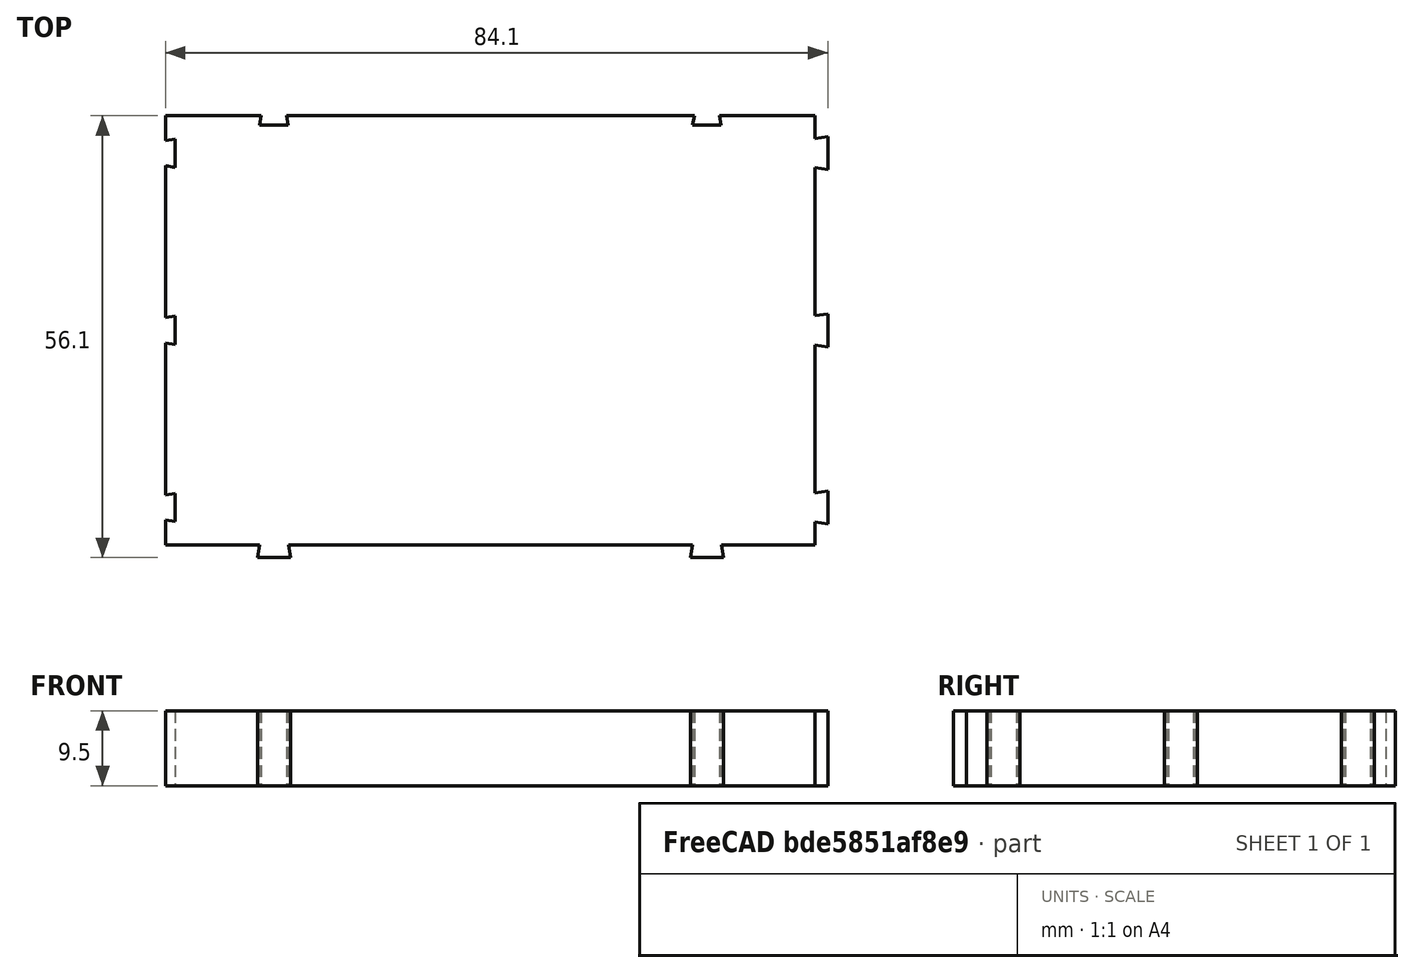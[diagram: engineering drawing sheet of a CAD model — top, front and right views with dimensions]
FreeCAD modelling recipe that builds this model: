
FCSTD DOCUMENT  (FreeCAD 0.18R15969 (Git))
Label: feature_breadboard
License: All rights reserved
LicenseURL: http://en.wikipedia.org/wiki/All_rights_reserved
objects: Sketcher::SketchObject×1, PartDesign::Pad×1, PartDesign::Body×1
note: 4 computed .brp shape members not serialized (recipe doc carries the construction recipe); baked Part::Feature solids carry a one-line shape summary decoded from their .brp

FEATURE [Sketcher::SketchObject] Sketch
  MapMode = 5
  Support = -> [XY_Plane]
  sketch-geometry (85):
    g0: LineSegment [constr] StartX=-41.25 StartY=-27.25 StartZ=0 EndX=41.25 EndY=-27.25 EndZ=0
    g1: LineSegment [constr] StartX=41.25 StartY=-27.25 StartZ=0 EndX=41.25 EndY=27.25 EndZ=0
    g2: LineSegment [constr] StartX=41.25 StartY=27.25 StartZ=0 EndX=-41.25 EndY=27.25 EndZ=0
    g3: LineSegment [constr] StartX=-41.25 StartY=27.25 StartZ=0 EndX=-41.25 EndY=-27.25 EndZ=0
    g4: LineSegment [constr] StartX=-41.25 StartY=27.25 StartZ=0 EndX=0 EndY=0 EndZ=0
    g5: LineSegment [constr] StartX=0 StartY=0 StartZ=0 EndX=41.25 EndY=27.25 EndZ=0
    g6: LineSegment [constr] StartX=0 StartY=0 StartZ=0 EndX=-41.25 EndY=-27.25 EndZ=0
    g7: LineSegment StartX=-41.25 StartY=27.25 StartZ=0 EndX=-29.1 EndY=27.25 EndZ=0
    g8: LineSegment StartX=-29.1 StartY=27.25 StartZ=0 EndX=-29.3 EndY=26.05 EndZ=0
    g9: LineSegment StartX=-29.3 StartY=26.05 StartZ=0 EndX=-25.7 EndY=26.05 EndZ=0
    g10: LineSegment StartX=-25.7 StartY=26.05 StartZ=0 EndX=-25.9 EndY=27.25 EndZ=0
    g11: LineSegment StartX=-25.9 StartY=27.25 StartZ=0 EndX=25.9 EndY=27.25 EndZ=0
    g12: LineSegment StartX=25.9 StartY=27.25 StartZ=0 EndX=25.7 EndY=26.05 EndZ=0
    g13: LineSegment StartX=25.7 StartY=26.05 StartZ=0 EndX=29.3 EndY=26.05 EndZ=0
    g14: LineSegment StartX=29.3 StartY=26.05 StartZ=0 EndX=29.1 EndY=27.25 EndZ=0
    g15: LineSegment StartX=29.1 StartY=27.25 StartZ=0 EndX=41.25 EndY=27.25 EndZ=0
    g16: LineSegment StartX=-41.25 StartY=27.25 StartZ=0 EndX=-41.25 EndY=24.1 EndZ=0
    g17: LineSegment StartX=-41.25 StartY=24.1 StartZ=0 EndX=-40.05 EndY=24.3 EndZ=0
    g18: LineSegment StartX=-40.05 StartY=24.3 StartZ=0 EndX=-40.05 EndY=20.7 EndZ=0
    g19: LineSegment StartX=-40.05 StartY=20.7 StartZ=0 EndX=-41.25 EndY=20.9 EndZ=0
    g20: LineSegment StartX=-41.25 StartY=20.9 StartZ=0 EndX=-41.25 EndY=1.6 EndZ=0
    g21: LineSegment StartX=-41.25 StartY=1.6 StartZ=0 EndX=-40.05 EndY=1.8 EndZ=0
    g22: LineSegment StartX=-40.05 StartY=1.8 StartZ=0 EndX=-40.05 EndY=-1.8 EndZ=0
    g23: LineSegment StartX=-40.05 StartY=-1.8 StartZ=0 EndX=-41.25 EndY=-1.6 EndZ=0
    g24: LineSegment [constr] StartX=-40.05 StartY=-1.8 StartZ=0 EndX=-41.25 EndY=1.6 EndZ=0
    g25: LineSegment [constr] StartX=-40.05 StartY=20.7 StartZ=0 EndX=-41.25 EndY=24.1 EndZ=0
    g26: LineSegment [constr] StartX=-29.3 StartY=26.05 StartZ=0 EndX=-25.9 EndY=27.25 EndZ=0
    g27: LineSegment [constr] StartX=25.7 StartY=26.05 StartZ=0 EndX=29.1 EndY=27.25 EndZ=0
    g28: LineSegment StartX=-41.25 StartY=-1.6 StartZ=0 EndX=-41.25 EndY=-20.9 EndZ=0
    g29: LineSegment StartX=-41.25 StartY=-20.9 StartZ=0 EndX=-40.05 EndY=-20.7 EndZ=0
    g30: LineSegment StartX=-40.05 StartY=-20.7 StartZ=0 EndX=-40.05 EndY=-24.3 EndZ=0
    g31: LineSegment StartX=-40.05 StartY=-24.3 StartZ=0 EndX=-41.25 EndY=-24.1 EndZ=0
    g32: LineSegment StartX=-41.25 StartY=-24.1 StartZ=0 EndX=-41.25 EndY=-27.25 EndZ=0
    g33: LineSegment [constr] StartX=-41.25 StartY=-20.9 StartZ=0 EndX=-40.05 EndY=-24.3 EndZ=0
    g34: LineSegment [constr] StartX=0 StartY=0 StartZ=0 EndX=-40.05 EndY=1.8 EndZ=0
    g35: LineSegment [constr] StartX=0 StartY=0 StartZ=0 EndX=-40.05 EndY=-1.8 EndZ=0
    g36: LineSegment [constr] StartX=-40.05 StartY=20.7 StartZ=0 EndX=0 EndY=22.5 EndZ=0
    g37: LineSegment [constr] StartX=0 StartY=22.5 StartZ=0 EndX=-40.05 EndY=24.3 EndZ=0
    g38: LineSegment [constr] StartX=-40.05 StartY=-20.7 StartZ=0 EndX=0 EndY=-22.5 EndZ=0
    g39: LineSegment [constr] StartX=-40.05 StartY=-24.3 StartZ=0 EndX=0 EndY=-22.5 EndZ=0
    g40: LineSegment [constr] StartX=0 StartY=-22.5 StartZ=0 EndX=0 EndY=0 EndZ=0
    g41: LineSegment [constr] StartX=0 StartY=0 StartZ=0 EndX=0 EndY=22.5 EndZ=0
    g42: LineSegment [constr] StartX=-29.3 StartY=26.05 StartZ=0 EndX=-27.5 EndY=-27.25 EndZ=0
    g43: LineSegment [constr] StartX=-27.5 StartY=-27.25 StartZ=0 EndX=-25.7 EndY=26.05 EndZ=0
    g44: LineSegment [constr] StartX=29.3 StartY=26.05 StartZ=0 EndX=27.5 EndY=-27.25 EndZ=0
    g45: LineSegment [constr] StartX=25.7 StartY=26.05 StartZ=0 EndX=27.5 EndY=-27.25 EndZ=0
    g46: LineSegment [constr] StartX=-27.5 StartY=-27.25 StartZ=0 EndX=0 EndY=0 EndZ=0
    g47: LineSegment [constr] StartX=0 StartY=0 StartZ=0 EndX=27.5 EndY=-27.25 EndZ=0
    g48: LineSegment StartX=41.25 StartY=27.25 StartZ=0 EndX=41.25 EndY=24.35 EndZ=0
    g49: LineSegment StartX=41.25 StartY=24.35 StartZ=0 EndX=42.85 EndY=24.6 EndZ=0
    g50: LineSegment StartX=42.85 StartY=24.6 StartZ=0 EndX=42.85 EndY=20.4 EndZ=0
    g51: LineSegment StartX=42.85 StartY=20.4 StartZ=0 EndX=41.25 EndY=20.65 EndZ=0
    g52: LineSegment StartX=41.25 StartY=20.65 StartZ=0 EndX=41.25 EndY=1.85 EndZ=0
    g53: LineSegment StartX=41.25 StartY=1.85 StartZ=0 EndX=42.85 EndY=2.1 EndZ=0
    g54: LineSegment StartX=42.85 StartY=2.1 StartZ=0 EndX=42.85 EndY=-2.1 EndZ=0
    g55: LineSegment StartX=42.85 StartY=-2.1 StartZ=0 EndX=41.25 EndY=-1.85 EndZ=0
    g56: LineSegment StartX=41.25 StartY=-1.85 StartZ=0 EndX=41.25 EndY=-20.65 EndZ=0
    g57: LineSegment StartX=41.25 StartY=-20.65 StartZ=0 EndX=42.85 EndY=-20.4 EndZ=0
    g58: LineSegment StartX=42.85 StartY=-20.4 StartZ=0 EndX=42.85 EndY=-24.6 EndZ=0
    g59: LineSegment StartX=42.85 StartY=-24.6 StartZ=0 EndX=41.25 EndY=-24.35 EndZ=0
    g60: LineSegment StartX=41.25 StartY=-24.35 StartZ=0 EndX=41.25 EndY=-27.25 EndZ=0
    g61: LineSegment StartX=-41.25 StartY=-27.25 StartZ=0 EndX=-29.35 EndY=-27.25 EndZ=0
    g62: LineSegment StartX=-29.35 StartY=-27.25 StartZ=0 EndX=-29.6 EndY=-28.85 EndZ=0
    g63: LineSegment StartX=-29.6 StartY=-28.85 StartZ=0 EndX=-25.4 EndY=-28.85 EndZ=0
    g64: LineSegment StartX=-25.4 StartY=-28.85 StartZ=0 EndX=-25.65 EndY=-27.25 EndZ=0
    g65: LineSegment StartX=-25.65 StartY=-27.25 StartZ=0 EndX=25.65 EndY=-27.25 EndZ=0
    g66: LineSegment StartX=25.65 StartY=-27.25 StartZ=0 EndX=25.4 EndY=-28.85 EndZ=0
    g67: LineSegment StartX=25.4 StartY=-28.85 StartZ=0 EndX=29.6 EndY=-28.85 EndZ=0
    g68: LineSegment StartX=29.6 StartY=-28.85 StartZ=0 EndX=29.35 EndY=-27.25 EndZ=0
    g69: LineSegment StartX=29.35 StartY=-27.25 StartZ=0 EndX=41.25 EndY=-27.25 EndZ=0
    g70: LineSegment [constr] StartX=-29.6 StartY=-28.85 StartZ=0 EndX=-27.5 EndY=-27.25 EndZ=0
    g71: LineSegment [constr] StartX=-27.5 StartY=-27.25 StartZ=0 EndX=-25.4 EndY=-28.85 EndZ=0
    g72: LineSegment [constr] StartX=25.4 StartY=-28.85 StartZ=0 EndX=27.5 EndY=-27.25 EndZ=0
    g73: LineSegment [constr] StartX=27.5 StartY=-27.25 StartZ=0 EndX=29.6 EndY=-28.85 EndZ=0
    g74: LineSegment [constr] StartX=42.85 StartY=-20.4 StartZ=0 EndX=0 EndY=-22.5 EndZ=0
    g75: LineSegment [constr] StartX=0 StartY=-22.5 StartZ=0 EndX=42.85 EndY=-24.6 EndZ=0
    g76: LineSegment [constr] StartX=42.85 StartY=-2.1 StartZ=0 EndX=0 EndY=0 EndZ=0
    g77: LineSegment [constr] StartX=0 StartY=0 StartZ=0 EndX=42.85 EndY=2.1 EndZ=0
    g78: LineSegment [constr] StartX=42.85 StartY=20.4 StartZ=0 EndX=0 EndY=22.5 EndZ=0
    g79: LineSegment [constr] StartX=0 StartY=22.5 StartZ=0 EndX=42.85 EndY=24.6 EndZ=0
    g80: LineSegment [constr] StartX=-29.35 StartY=-27.25 StartZ=0 EndX=-25.4 EndY=-28.85 EndZ=0
    g81: LineSegment [constr] StartX=25.65 StartY=-27.25 StartZ=0 EndX=29.6 EndY=-28.85 EndZ=0
    g82: LineSegment [constr] StartX=41.25 StartY=-24.35 StartZ=0 EndX=42.85 EndY=-20.4 EndZ=0
    g83: LineSegment [constr] StartX=41.25 StartY=-1.85 StartZ=0 EndX=42.85 EndY=2.1 EndZ=0
    g84: LineSegment [constr] StartX=41.25 StartY=20.65 StartZ=0 EndX=42.85 EndY=24.6 EndZ=0
  constraints (226):
    c: Coincident(g0,g1)
    c: Coincident(g1,g2)
    c: Coincident(g2,g3)
    c: Coincident(g3,g0)
    c: Horizontal(g0)
    c: Horizontal(g2)
    c: Vertical(g1)
    c: Vertical(g3)
    c: DistanceX(g2,g2) = 82.5
    c: DistanceY(g1,g1) = 54.5
    c: Coincident(g4,g2)
    c: Coincident(g5,g4)
    c: Coincident(g5,g1)
    c: Coincident(g6,g4)
    c: Coincident(g6,g0)
    c: Equal(g6,g4)
    c: Equal(g4,g5)
    c: Coincident(g2,g7)
    c: Coincident(g7,g8)
    c: Coincident(g8,g9)
    c: Horizontal(g9)
    c: Coincident(g9,g10)
    c: Coincident(g10,g11)
    c: Coincident(g11,g12)
    c: Coincident(g12,g13)
    c: Horizontal(g13)
    c: Coincident(g13,g14)
    c: Coincident(g14,g15)
    c: Coincident(g15,g1)
    c: PointOnObject(g14,g2)
    c: PointOnObject(g11,g2)
    c: PointOnObject(g10,g2)
    c: PointOnObject(g7,g2)
    c: Equal(g8,g10)
    c: Equal(g12,g14)
    c: Coincident(g7,g16)
    c: Coincident(g16,g17)
    c: Coincident(g17,g18)
    c: Vertical(g18)
    c: Coincident(g18,g19)
    c: Coincident(g19,g20)
    c: Coincident(g20,g21)
    c: Coincident(g21,g22)
    c: Vertical(g22)
    c: Coincident(g22,g23)
    c: PointOnObject(g23,g3)
    c: PointOnObject(g20,g3)
    c: PointOnObject(g19,g3)
    c: PointOnObject(g16,g3)
    c: Equal(g8,g17)
    c: Equal(g17,g19)
    c: Equal(g19,g21)
    c: Equal(g21,g23)
    c: Equal(g22,g18)
    c: Equal(g18,g9)
    c: Equal(g9,g13)
    c: Coincident(g24,g22)
    c: Coincident(g24,g20)
    c: Coincident(g25,g18)
    c: Coincident(g25,g16)
    c: Coincident(g26,g8)
    c: Coincident(g26,g10)
    c: Coincident(g27,g12)
    c: Coincident(g27,g14)
    c: Equal(g26,g27)
    c: Equal(g27,g25)
    c: Equal(g25,g24)
    c: Coincident(g23,g28)
    c: Coincident(g28,g29)
    c: Coincident(g29,g30)
    c: Vertical(g30)
    c: Coincident(g30,g31)
    c: Coincident(g31,g32)
    c: Coincident(g32,g0)
    c: PointOnObject(g31,g3)
    c: PointOnObject(g28,g3)
    c: Equal(g30,g22)
    c: Equal(g29,g31)
    c: Equal(g31,g23)
    c: Coincident(g33,g28)
    c: Coincident(g33,g30)
    c: Equal(g33,g24)
    c: Coincident(g34,g4)
    c: Coincident(g34,g21)
    c: Coincident(g35,g4)
    c: Coincident(g35,g22)
    c: Coincident(g36,g18)
    c: PointOnObject(g36,g-2)
    c: Coincident(g37,g36)
    c: Coincident(g37,g17)
    c: Coincident(g38,g29)
    c: PointOnObject(g38,g-2)
    c: Coincident(g39,g30)
    c: Coincident(g39,g38)
    c: Coincident(g40,g38)
    c: Coincident(g40,g4)
    c: Coincident(g41,g4)
    c: Coincident(g41,g36)
    c: Equal(g41,g40)
    c: DistanceY(g38,g36) = 45
    c: DistanceY(g19,g16) = 3.2
    c: DistanceY(g18,g18) = 3.6
    c: DistanceX(g19,g19) = 1.2
    c: Coincident(g42,g8)
    c: PointOnObject(g42,g0)
    c: Coincident(g43,g42)
    c: Coincident(g43,g9)
    c: Coincident(g44,g13)
    c: PointOnObject(g44,g0)
    c: Coincident(g45,g12)
    c: Coincident(g45,g44)
    c: Equal(g44,g45)
    c: Equal(g45,g42)
    c: Equal(g42,g43)
    c: Coincident(g46,g42)
    c: Coincident(g46,g4)
    c: Coincident(g47,g4)
    c: Coincident(g47,g44)
    c: Equal(g46,g47)
    c: DistanceX(g42,g44) = 55
    c: Coincident(g15,g48)
    c: Coincident(g48,g49)
    c: Coincident(g49,g50)
    c: Vertical(g50)
    c: Coincident(g50,g51)
    c: Coincident(g51,g52)
    c: Coincident(g52,g53)
    c: Coincident(g53,g54)
    c: Vertical(g54)
    c: Coincident(g54,g55)
    c: Coincident(g55,g56)
    c: Coincident(g56,g57)
    c: Coincident(g57,g58)
    c: Vertical(g58)
    c: Coincident(g58,g59)
    c: Coincident(g59,g60)
    c: Coincident(g60,g0)
    c: PointOnObject(g56,g1)
    c: PointOnObject(g59,g1)
    c: PointOnObject(g55,g1)
    c: PointOnObject(g52,g1)
    c: PointOnObject(g51,g1)
    c: PointOnObject(g48,g1)
    c: Coincident(g32,g61)
    c: Coincident(g61,g62)
    c: Coincident(g62,g63)
    c: Horizontal(g63)
    c: Coincident(g63,g64)
    c: Coincident(g65,g66)
    c: Coincident(g66,g67)
    c: Horizontal(g67)
    c: Coincident(g67,g68)
    c: Coincident(g68,g69)
    c: Coincident(g69,g60)
    c: PointOnObject(g61,g0)
    c: PointOnObject(g64,g0)
    c: PointOnObject(g65,g0)
    c: PointOnObject(g68,g0)
    c: Equal(g67,g58)
    c: Equal(g58,g54)
    c: Equal(g54,g50)
    c: Equal(g64,g62)
    c: Equal(g66,g68)
    c: Equal(g68,g59)
    c: Equal(g59,g57)
    c: Equal(g57,g55)
    c: Equal(g55,g53)
    c: Equal(g53,g51)
    c: Equal(g51,g49)
    c: Coincident(g70,g62)
    c: Coincident(g70,g42)
    c: Coincident(g71,g42)
    c: Coincident(g71,g63)
    c: Coincident(g65,g64)
    c: Coincident(g72,g66)
    c: Coincident(g72,g44)
    c: Coincident(g73,g44)
    c: Coincident(g73,g67)
    c: Coincident(g74,g57)
    c: Coincident(g74,g38)
    c: Coincident(g75,g38)
    c: Coincident(g75,g58)
    c: Coincident(g76,g54)
    c: Coincident(g76,g4)
    c: Coincident(g77,g4)
    c: Coincident(g77,g53)
    c: Coincident(g78,g50)
    c: Coincident(g78,g36)
    c: Coincident(g79,g36)
    c: Coincident(g79,g49)
    c: Equal(g75,g74)
    c: Equal(g76,g77)
    c: Equal(g78,g79)
    c: Equal(g70,g71)
    c: Equal(g72,g73)
    c: Equal(g63,g67)
    c: DistanceY(g62,g61) = 1.6
    c: Equal(g62,g64)
    c: Equal(g64,g66)
    c: Equal(g66,g68)
    c: Equal(g68,g59)
    c: Equal(g59,g57)
    c: Equal(g57,g55)
    c: Equal(g55,g53)
    c: Equal(g53,g51)
    c: Equal(g51,g49)
    c: Coincident(g80,g61)
    c: Coincident(g80,g63)
    c: Coincident(g81,g65)
    c: Coincident(g81,g67)
    c: Coincident(g82,g59)
    c: Coincident(g82,g57)
    c: Coincident(g83,g55)
    c: Coincident(g83,g53)
    c: Coincident(g84,g51)
    c: Coincident(g84,g49)
    c: Equal(g84,g83)
    c: Equal(g83,g82)
    c: Equal(g82,g81)
    c: Equal(g81,g80)
    c: DistanceX(g63,g63) = 4.2
    c: DistanceX(g61,g64) = 3.7
    c: Equal(g35,g34)
    c: Equal(g37,g36)
    c: Equal(g39,g38)
    c: Coincident(g4,g-1)
FEATURE [PartDesign::Pad] Pad
  Length = 9.5
  Length2 = 100
  Profile = -> Sketch
  Refine = true
  Reversed = true
  Type = 0
FEATURE [PartDesign::Body] Body  label="feature_breadboard"
  Group = -> [Sketch,Pad]
  Origin = -> Origin
  Tip = -> Pad
